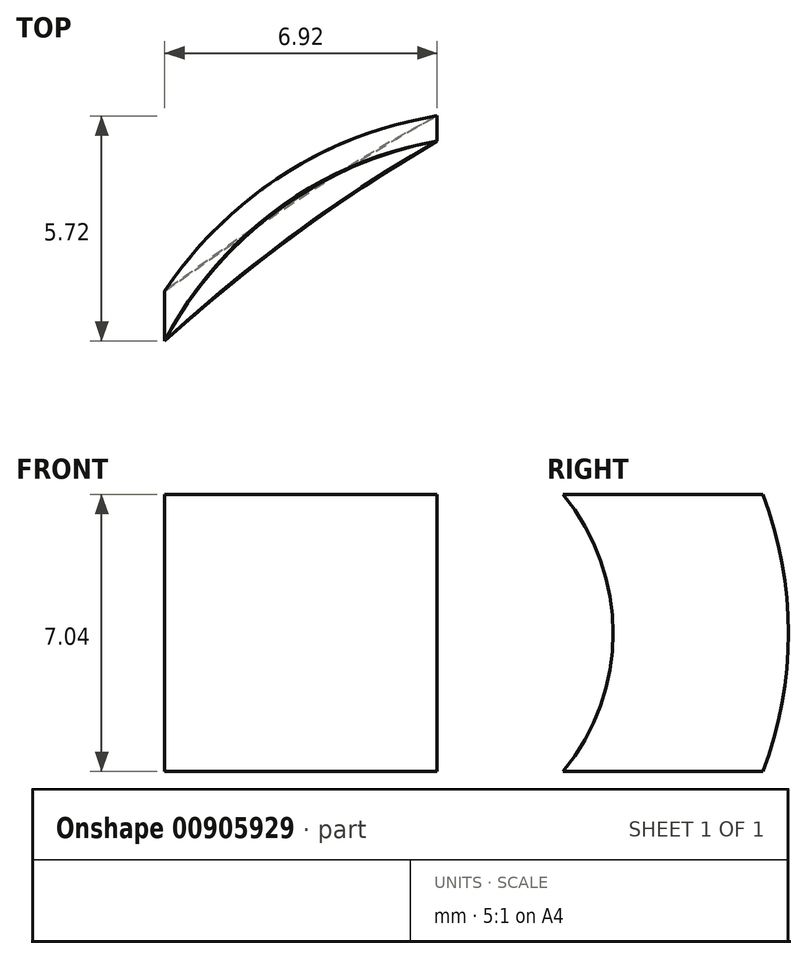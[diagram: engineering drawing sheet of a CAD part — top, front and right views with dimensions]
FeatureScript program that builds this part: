
annotation { "Feature Type Name" : "Feature", "Feature Type Description" : "" }
export const myFeature = defineFeature(function(context is Context, id is Id, definition is map)
    precondition{}
    {
        {
            var Q0;
            Q0=qCreatedBy(makeId("Top.planeOp"),FACE);
            var sketch = newSketch(context, id + "F0", { "sketchPlane" : qUnion([Q0])});
            skLineSegment(sketch, "E0", {"start": v(0, 0) * mm, "end": v(6.92, 0) * mm, "construction": true});
            skLineSegment(sketch, "E1", {"start": v(6.92, 0) * mm, "end": v(6.92, 5.08) * mm, "construction": true});
            skLineSegment(sketch, "E2", {"start": v(0, 5.08) * mm, "end": v(6.92, 5.08) * mm, "construction": true});
            skLineSegment(sketch, "E3", {"start": v(0, 5.08) * mm, "end": v(0, 0) * mm, "construction": true});
            skArc(sketch, "E4", {"start": v(6.92, 5.08) * mm, "mid": v(2.86, 3.35) * mm, "end": v(0, 0) * mm});
            skArc(sketch, "E5", {"start": v(6.92, 5.08) * mm, "mid": v(3.31, 2.74) * mm, "end": v(0, 0) * mm});
            skSolve(sketch);
        }
        {
            var Q0;
            Q0=qCreatedBy(makeId("Top.planeOp"),FACE);
            cPlane(context, id + "F1", {"entities" : qUnion([Q0]), "cplaneType" : CPlaneType.OFFSET, "offset" : 7.04 * mm, "width" : 152.4 * mm, "height" : 152.4 * mm});
        }
        {
            var Q0;
            Q0=qCreatedBy(id+"F1.planeOp",FACE);
            var sketch = newSketch(context, id + "F2", { "sketchPlane" : qUnion([Q0])});
            skArc(sketch, "E6", {"start": v(6.92, 5.08) * mm, "mid": v(2.88, 3.33) * mm, "end": v(0, 0) * mm});
            skArc(sketch, "E7", {"start": v(6.92, 5.08) * mm, "mid": v(3.33, 2.72) * mm, "end": v(0, 0) * mm});
            skSolve(sketch);
        }
        {
            var Q0;
            Q0=qCreatedBy(makeId("Right.planeOp"),FACE);
            var sketch = newSketch(context, id + "F3", { "sketchPlane" : qUnion([Q0])});
            skLineSegment(sketch, "E8", {"start": v(0, 7.04) * mm, "end": v(0, 0) * mm, "construction": true});
            skArc(sketch, "E9", {"start": v(0, 0) * mm, "mid": v(1.27, 3.52) * mm, "end": v(0, 7.04) * mm});
            skSolve(sketch);
        }
        {
            var Q0;
            Q0=makeQuery(id+"F0.imprint","IMPRINT",FACE,{"disambiguationData":[TD([[makeQuery(id+"F0.imprint","IMPRINT",EDGE,{"derivedFrom":sQuery(id+"F0.wireOp",EDGE,"E4")}),1.0]])]});
            var Q1;
            Q1=makeQuery(id+"F2.imprint","IMPRINT",FACE,{"disambiguationData":[TD([[makeQuery(id+"F2.imprint","IMPRINT",EDGE,{"derivedFrom":sQuery(id+"F2.wireOp",EDGE,"E6")}),1.0]])]});
            var Q2;
            Q2=sQuery(id+"F3.wireOp",EDGE,"E9");
            sweep(context, id + "F4", {"profiles" : qUnion([Q0, Q1]), "path" : qUnion([Q2])});
        }
        {
            var Q0;
            Q0=qCreatedBy(makeId("Right.planeOp"),FACE);
            var sketch = newSketch(context, id + "F5", { "sketchPlane" : qUnion([Q0])});
            skLineSegment(sketch, "E10.bottom", {"start": v(-2.96, 0) * mm, "end": v(9.28, 0) * mm});
            skLineSegment(sketch, "E10.top", {"start": v(-2.96, -6.43) * mm, "end": v(9.28, -6.43) * mm});
            skLineSegment(sketch, "E10.left", {"start": v(-2.96, 0) * mm, "end": v(-2.96, -6.43) * mm});
            skLineSegment(sketch, "E10.right", {"start": v(9.28, 0) * mm, "end": v(9.28, -6.43) * mm});
            skLineSegment(sketch, "E11.bottom", {"start": v(-2.96, 7.04) * mm, "end": v(8.53, 7.04) * mm});
            skLineSegment(sketch, "E11.top", {"start": v(-2.96, 12.68) * mm, "end": v(8.53, 12.68) * mm});
            skLineSegment(sketch, "E11.left", {"start": v(-2.96, 7.04) * mm, "end": v(-2.96, 12.68) * mm});
            skLineSegment(sketch, "E11.right", {"start": v(8.53, 7.04) * mm, "end": v(8.53, 12.68) * mm});
            skSolve(sketch);
        }
        {
            var Q0;
            Q0 = qSketchRegion(id + "F5", true);
            extrude(context, id + "F6", {"entities" : qUnion([Q0]), "operationType" : NewBodyOperationType.REMOVE, "depth" : 32 * mm, "offsetDistance" : 25.4 * mm});
        }
    });
